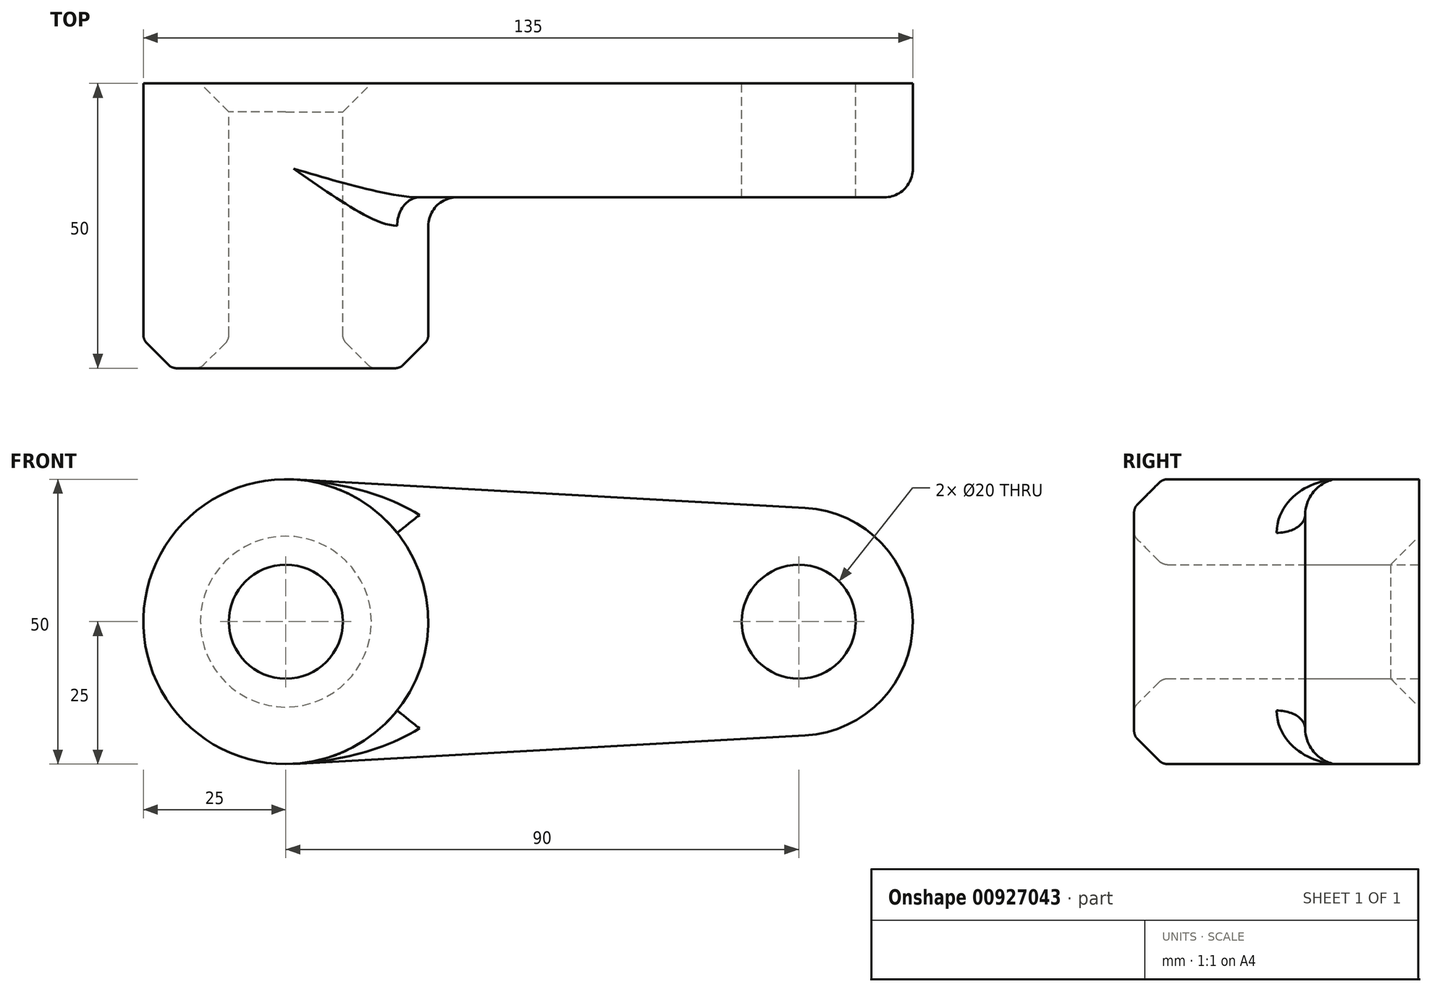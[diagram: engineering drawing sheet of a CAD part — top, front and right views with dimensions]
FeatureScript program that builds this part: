
annotation { "Feature Type Name" : "Feature", "Feature Type Description" : "" }
export const myFeature = defineFeature(function(context is Context, id is Id, definition is map)
    precondition{}
    {
        {
            var Q0;
            Q0=qCreatedBy(makeId("Front.planeOp"),FACE);
            var sketch = newSketch(context, id + "F0", { "sketchPlane" : qUnion([Q0])});
            skCircle(sketch, "E0", {"center": v(0, 0) * mm, "radius": 25 * mm});
            skCircle(sketch, "E1", {"center": v(90, 0) * mm, "radius": 20 * mm});
            skLineSegment(sketch, "E2", {"start": v(1.39, -24.96) * mm, "end": v(91.11, -19.97) * mm});
            skLineSegment(sketch, "E3", {"start": v(1.39, 24.96) * mm, "end": v(91.11, 19.97) * mm});
            skCircle(sketch, "E4", {"center": v(0, 0) * mm, "radius": 10 * mm});
            skCircle(sketch, "E5", {"center": v(90, 0) * mm, "radius": 10 * mm});
            skFitSpline(sketch, "E6", {"points": [v(1.39, 24.96) * mm, v(30.95, 74.52) * mm, v(88.19, 83.04) * mm], "startDerivative": vector(49.63, 73.46) * mm, "endDerivative": vector(103.51, -22.93) * mm});
            skSolve(sketch);
        }
        {
            var Q0;
            Q0 = qSketchRegion(id + "F0", true);
            extrude(context, id + "F1", {"entities" : qUnion([Q0]), "depth" : 20 * mm, "offsetDistance" : 25 * mm});
        }
        {
            var Q0;
            Q0=makeQuery(id+"F0.imprint","IMPRINT",FACE,{"disambiguationData":[TD([[makeQuery(id+"F0.imprint","IMPRINT",EDGE,{"derivedFrom":sQuery(id+"F0.wireOp",EDGE,"E4")}),-1.0]])]});
            extrude(context, id + "F2", {"entities" : qUnion([Q0]), "operationType" : NewBodyOperationType.ADD, "depth" : 50 * mm, "offsetDistance" : 25 * mm});
        }
        {
            var Q0;
            Q0=makeQuery(id+"F2.opExtrude","CAP_EDGE",EDGE,{"disambiguationData":[OSD([sQuery(id+"F0.wireOp",EDGE,"E0")])],"isStart":false});
            var Q1;
            {var subQ0=sQuery(id+"F0.wireOp",EDGE,"E4");Q1=makeQuery(id+"F2.boolean.opBoolean","MERGE",FACE,{"derivedFrom":[makeQuery(id+"F1.opExtrude","SWEPT_FACE",FACE,{"disambiguationData":[OSD([subQ0])]}),makeQuery(id+"F2.opExtrude","SWEPT_FACE",FACE,{"disambiguationData":[OSD([subQ0])]})]});}
            chamfer(context, id + "F3", {"entities" : qUnion([Q0, Q1]), "width" : 5 * mm, "tangentPropagation" : true});
        }
        {
            var Q0;
            Q0=makeQuery(id+"F1.opExtrude","CAP_EDGE",EDGE,{"disambiguationData":[OSD([sQuery(id+"F0.wireOp",EDGE,"E2")])],"isStart":false});
            var Q1;
            {var subQ0=sQuery(id+"F0.wireOp",EDGE,"E0");Q1=makeQuery(id+"F2.boolean.opBoolean","INTERSECT",EDGE,{"derivedFrom":[makeQuery(id+"F1.opExtrude","CAP_FACE",FACE,{"disambiguationData":[OSD([subQ0,sQuery(id+"F0.wireOp",EDGE,"E1"),sQuery(id+"F0.wireOp",EDGE,"E2"),sQuery(id+"F0.wireOp",EDGE,"E3"),sQuery(id+"F0.wireOp",EDGE,"E4"),sQuery(id+"F0.wireOp",EDGE,"E5")])],"isStart":false}),makeQuery(id+"F2.opExtrude","SWEPT_FACE",FACE,{"disambiguationData":[OSD([subQ0])]})]});}
            fillet(context, id + "F4", {"entities" : qUnion([Q0, Q1]), "radius" : 5 * mm, "tangentPropagation" : true, "allowEdgeOverflow" : false});
        }
        {
            var Q0;
            {var subQ0=sQuery(id+"F0.wireOp",EDGE,"E0");Q0=makeQuery(id+"F3.opChamfer","BLEND_EDGE",EDGE,{"blendedFrom":[makeQuery(id+"F2.opExtrude","CAP_EDGE",EDGE,{"disambiguationData":[OSD([subQ0])],"isStart":false}),makeQuery(id+"F2.boolean.opBoolean","MERGE",FACE,{"derivedFrom":[makeQuery(id+"F1.opExtrude","SWEPT_FACE",FACE,{"disambiguationData":[OSD([subQ0])]}),makeQuery(id+"F2.opExtrude","SWEPT_FACE",FACE,{"disambiguationData":[OSD([subQ0])]})]})],"blendedInto":[makeQuery(id+"F2.boolean.opBoolean","MERGE",FACE,{"derivedFrom":[makeQuery(id+"F1.opExtrude","SWEPT_FACE",FACE,{"disambiguationData":[OSD([subQ0])]}),makeQuery(id+"F2.opExtrude","SWEPT_FACE",FACE,{"disambiguationData":[OSD([subQ0])]})]})]});}
            var Q1;
            {var subQ0=sQuery(id+"F0.wireOp",EDGE,"E0");Q1=makeQuery(id+"F3.opChamfer","BLEND_EDGE",EDGE,{"blendedFrom":[makeQuery(id+"F2.opExtrude","CAP_EDGE",EDGE,{"disambiguationData":[OSD([subQ0])],"isStart":false}),makeQuery(id+"F2.opExtrude","CAP_FACE",FACE,{"disambiguationData":[OSD([subQ0,sQuery(id+"F0.wireOp",EDGE,"E4")])],"isStart":false})],"blendedInto":[makeQuery(id+"F2.opExtrude","CAP_FACE",FACE,{"disambiguationData":[OSD([subQ0,sQuery(id+"F0.wireOp",EDGE,"E4")])],"isStart":false})]});}
            var Q2;
            {var subQ0=sQuery(id+"F0.wireOp",EDGE,"E4");Q2=makeQuery(id+"F3.opChamfer","BLEND_EDGE",EDGE,{"blendedFrom":[makeQuery(id+"F2.opExtrude","CAP_EDGE",EDGE,{"disambiguationData":[OSD([subQ0])],"isStart":false}),makeQuery(id+"F2.opExtrude","CAP_FACE",FACE,{"disambiguationData":[OSD([sQuery(id+"F0.wireOp",EDGE,"E0"),subQ0])],"isStart":false})],"blendedInto":[makeQuery(id+"F2.opExtrude","CAP_FACE",FACE,{"disambiguationData":[OSD([sQuery(id+"F0.wireOp",EDGE,"E0"),subQ0])],"isStart":false})]});}
            var Q3;
            {var subQ0=sQuery(id+"F0.wireOp",EDGE,"E4");Q3=makeQuery(id+"F3.opChamfer","BLEND_EDGE",EDGE,{"blendedFrom":[makeQuery(id+"F2.opExtrude","CAP_EDGE",EDGE,{"disambiguationData":[OSD([subQ0])],"isStart":false}),makeQuery(id+"F2.boolean.opBoolean","MERGE",FACE,{"derivedFrom":[makeQuery(id+"F1.opExtrude","SWEPT_FACE",FACE,{"disambiguationData":[OSD([subQ0])]}),makeQuery(id+"F2.opExtrude","SWEPT_FACE",FACE,{"disambiguationData":[OSD([subQ0])]})]})],"blendedInto":[makeQuery(id+"F2.boolean.opBoolean","MERGE",FACE,{"derivedFrom":[makeQuery(id+"F1.opExtrude","SWEPT_FACE",FACE,{"disambiguationData":[OSD([subQ0])]}),makeQuery(id+"F2.opExtrude","SWEPT_FACE",FACE,{"disambiguationData":[OSD([subQ0])]})]})]});}
            fillet(context, id + "F5", {"entities" : qUnion([Q0, Q1, Q2, Q3]), "radius" : 2 * mm, "tangentPropagation" : true, "allowEdgeOverflow" : false});
        }
    });
